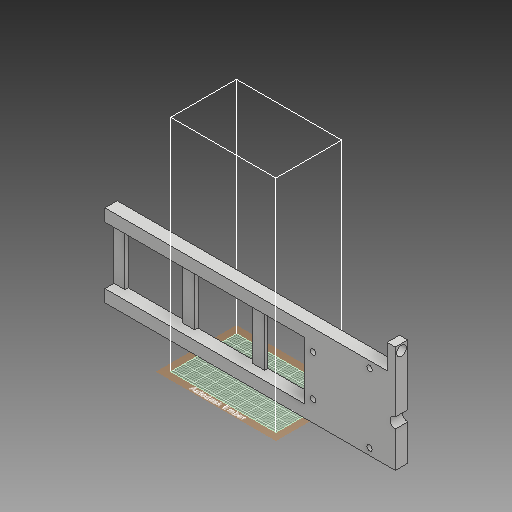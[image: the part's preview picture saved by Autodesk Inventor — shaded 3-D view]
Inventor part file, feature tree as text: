
AUTODESK INVENTOR PART (.ipt)
format: ipt  version: 2018 (Build 220112000, 112)  size: 895,488 bytes
history: native  units: mm
features: sketch x56, extrude x42, fillet x12, hole x8
ambient origin geometry x8: Origin, YZ Plane, XZ Plane, XY Plane, X Axis, Y Axis, Z Axis, Center Point
bodies: Solid1 (feature_tree)
feature tree (118):
  extrude  "Extrusion1"  Depth=50.0mm
  hole  "Hole1"  [1 undecoded]
  hole  "Hole2"  [1 undecoded]
  extrude  "Extrusion2"  Depth=2.0mm
  extrude  "Extrusion3"  Depth=2.0mm
  extrude  "Extrusion4"  Depth=5.0mm
  sketch  "Sketch7"  dims[d25=10.0mm d26=5.0mm]
  extrude  "Extrusion5"  Depth=5.0mm
  extrude  "Extrusion6"  Depth=35.0mm
  extrude  "Extrusion7"  Depth=35.0mm
  extrude  "Extrusion8"  Depth=35.0mm
  extrude  "Extrusion9"  Depth=2.0mm TaperAngle=0.0deg
  extrude  "Extrusion10"  Depth=7.5mm TaperAngle=0.0deg
  extrude  "Extrusion11"  Depth=10.0mm
  extrude  "Extrusion12"  Depth=7.5mm
  fillet  "Fillet1"  Radius=7.5mm
  fillet  "Fillet2"  Radius=25.0mm
  fillet  "Fillet3"  Radius=3.0mm
  fillet  "Fillet4"  Radius=3.2mm
  fillet  "Fillet5"  Radius=2.1mm
  fillet  "Fillet6"  Radius=5.5mm
  extrude  "Extrusion13"  Depth=92.5mm TaperAngle=0.0deg
  sketch  "Sketch17"  dims[d58=4.25mm d59=241.0mm d60=0.0mm]
  hole  "Hole3"  [1 undecoded]
  hole  "Hole4"  [1 undecoded]
  extrude  "Extrusion14"  Depth=5.0mm
  extrude  "Extrusion15"  Depth=2.5mm TaperAngle=0.0deg
  extrude  "Extrusion16"  Depth=6.35mm
  extrude  "Extrusion17"  Depth=2.5mm
  extrude  "Extrusion18"  Depth=14.55mm TaperAngle=0.0deg
  extrude  "Extrusion19"  Depth=0.1mm
  extrude  "Extrusion20"  Depth=3.25mm
  extrude  "Extrusion21"  Depth=3.25mm
  hole  "Hole5"  [1 undecoded]
  extrude  "Extrusion22"  Depth=2.0mm
  extrude  "Extrusion23"  Depth=15.0mm
  extrude  "Extrusion24"  Depth=10.0mm TaperAngle=0.0deg
  hole  "Hole6"  [1 undecoded]
  extrude  "Extrusion25"  Depth=100.0mm TaperAngle=0.0deg
  extrude  "Extrusion26"  Depth=2.0mm TaperAngle=0.0deg
  extrude  "Extrusion27"  Depth=3.3mm
  extrude  "Extrusion28"  Depth=3.3mm
  hole  "Hole7"  [1 undecoded]
  extrude  "Extrusion29"  Depth=2.0mm
  extrude  "Extrusion30"  Depth=17.0mm
  hole  "Hole8"  [1 undecoded]
  extrude  "Extrusion31"  Depth=21.0mm
  extrude  "Extrusion32"  Depth=10.0mm
  fillet  "Fillet7"  Radius=3.3mm
  fillet  "Fillet8"  Radius=10.0mm
  extrude  "Extrusion33"  Depth=5.0mm
  extrude  "Extrusion34"  Depth=5.0mm
  sketch  "Sketch45"  dims[d149=10.0mm d150=17.5mm d151=0.0mm]
  sketch  "Sketch46"  dims[d152=5.0mm]
  extrude  "Extrusion35"  Depth=10.0mm TaperAngle=0.0deg
  extrude  "Extrusion36"  Depth=2.0mm TaperAngle=0.0deg
  extrude  "Extrusion37"  Depth=3.75mm
  extrude  "Extrusion38"  Depth=3.75mm
  fillet  "Fillet9"  Radius=3.75mm
  extrude  "Extrusion39"  Depth=10.0mm TaperAngle=0.0deg
  fillet  "Fillet10"  Radius=2.0mm
  sketch  "Sketch52"  dims[d181=5.0mm d182=15.0mm d183=0.0mm]
  extrude  "Extrusion40"  Depth=15.0mm TaperAngle=0.0deg
  sketch  "Sketch54"  dims[d185=6.0mm d186=6.0mm d187=4.0mm d188=2.0mm d189=90.0deg d190=15.0mm d191=0.0mm d192=17.5mm d193=0.0mm]
  extrude  "Extrusion41"  Depth=15.0mm TaperAngle=0.0deg
  extrude  "Extrusion42"  Depth=47.5mm
  fillet  "Fillet11"  Radius=20.0mm
  fillet  "Fillet12"  Radius=5.0mm
  sketch  "Sketch1"  dims[d0=50.0mm d1=50.0mm]
  sketch  "Sketch2"  dims[d2=240.0mm d3=7.5mm]
  sketch  "Sketch3"  dims[d4=7.5mm d5=7.5mm d6=0.0mm]
  sketch  "Sketch4"  dims[d7=6.35mm d8=6.0mm d9=4.0mm d10=2.0mm d11=90.0deg d12=8.0mm d13=20.594885mm d14=25.0mm]
  sketch  "Sketch5"  dims[d15=3.3mm d16=6.0mm d17=4.0mm d18=2.0mm d19=90.0deg d20=8.0mm d21=20.594885mm d22=25.0mm]
  sketch  "Sketch6"  dims[d23=180.0deg d24=5.0mm]
  sketch  "Sketch8"  dims[d27=17.5mm d28=0.0mm d30=35.0mm]
  sketch  "Sketch9"  dims[d31=35.0mm d32=35.0mm]
  sketch  "Sketch10"  dims[d33=35.0mm d34=35.0mm]
  sketch  "Sketch11"  dims[d35=35.0mm d36=2.0mm d37=0.0mm]
  sketch  "Sketch12"  dims[d38=10.0mm d39=7.5mm d40=0.0mm]
  sketch  "Sketch13"  dims[d41=100.0mm d42=10.0mm]
  sketch  "Sketch14"  dims[d43=7.5mm d44=0.0mm d45=7.5mm d46=7.5mm d47=25.0mm d48=0.0mm d49=3.0mm d50=3.2mm d51=2.1mm d52=5.5mm]
  sketch  "Sketch15"  dims[d53=3.3mm d54=92.5mm d55=0.0mm]
  sketch  "Sketch16"  dims[d56=5.5mm d57=3.3mm]
  sketch  "Sketch18"  dims[d61=4.44mm d62=5.0mm]
  sketch  "Sketch19"  dims[d63=2.5mm d64=91.25mm d65=0.0mm]
  sketch  "Sketch20"  dims[d66=30.0mm d67=6.35mm]
  sketch  "Sketch21"  dims[d68=3.8mm d69=0.0mm d70=2.5mm]
  sketch  "Sketch22"  dims[d71=14.55mm d72=0.0mm d73=14.55mm d74=0.0mm]
  sketch  "Sketch23"  dims[d75=0.1mm d76=0.1mm]
  sketch  "Sketch24"  dims[d77=3.25mm d78=3.25mm]
  sketch  "Sketch25"  dims[d79=3.25mm d80=3.25mm]
  sketch  "Sketch26"  dims[d81=35.0mm d82=10.0mm]
  sketch  "Sketch27"  dims[d83=2.0mm d84=0.0mm d85=3.6mm]
  sketch  "Sketch28"  dims[d86=3.6mm]
  sketch  "Sketch29"  dims[d87=3.3mm d88=6.0mm d89=4.0mm d90=2.0mm d91=90.0deg d92=15.0mm d93=20.594885mm]
  sketch  "Sketch30"  dims[d94=3.3mm d95=6.0mm d96=4.0mm d97=2.0mm d98=90.0deg d99=15.0mm d100=20.594885mm d101=6.0mm]
  sketch  "Sketch31"  dims[d102=20.0mm d103=0.0mm d104=10.0mm d105=0.0mm]
  sketch  "Sketch32"  dims[d106=2.0mm d107=0.0mm d108=4.0mm]
  sketch  "Sketch33"  dims[d109=100.0mm d110=0.0mm d111=100.0mm d112=0.0mm]
  sketch  "Sketch34"  dims[d113=5.0mm d114=2.0mm d115=0.0mm]
  sketch  "Sketch35"  dims[d116=3.3mm d117=3.3mm]
  sketch  "Sketch36"  dims[d118=3.3mm d119=3.3mm]
  sketch  "Sketch37"  dims[d120=2.0mm d121=0.0mm d122=5.5mm d123=0.0mm]
  sketch  "Sketch38"  dims[d124=3.3mm d125=6.0mm d126=4.0mm d127=2.0mm d128=90.0deg d129=8.0mm d130=20.594885mm d131=42.0mm]
  sketch  "Sketch39"  dims[d132=17.0mm d133=21.0mm]
  sketch  "Sketch40"  dims[d135=8.5mm d136=15.825mm]
  sketch  "Sketch41"  dims[d137=3.5mm d138=21.0mm]
  sketch  "Sketch42"  dims[d139=3.3mm d140=3.3mm d141=3.3mm d142=10.0mm d143=0.0mm]
  sketch  "Sketch43"  dims[d144=7.5mm d145=0.0mm d146=5.0mm]
  sketch  "Sketch44"  dims[d147=10.0mm d148=5.0mm]
  sketch  "Sketch47"  dims[d153=7.0mm d154=6.0mm d155=4.0mm d156=2.0mm d157=90.0deg d158=8.0mm d159=20.594885mm d160=17.5mm d161=0.0mm]
  sketch  "Sketch48"  dims[d162=170.5mm d163=0.0mm d164=3.75mm]
  sketch  "Sketch49"  dims[d165=3.75mm d166=3.75mm d167=3.75mm]
  sketch  "Sketch50"  dims[d168=10.0mm d169=0.0mm d170=100.0mm d171=0.0mm]
  sketch  "Sketch51"  dims[d172=5.0mm d173=6.0mm d174=4.0mm d175=2.0mm d176=90.0deg d177=15.0mm d178=0.0mm d179=2.0mm d180=0.0mm]
  sketch  "Sketch53"  dims[d184=7.5mm]
  sketch  "Sketch55"  dims[d194=23.75mm d195=47.5mm d200=20.0mm d203=5.0mm]
  sketch  "Sketch56"  dims[d204=5.0mm d205=29.0mm d206=29.0mm d207=7.5mm d208=0.0mm d209=4.0mm d210=4.0mm d211=2.0mm d212=0.0mm d213=12.0mm d214=2.0mm d215=0.0mm d216=7.5mm d217=7.5mm d218=20.0mm d219=0.0mm d220=20.0mm d221=3.3mm d222=20.0mm d223=0.0mm d224=100.0mm d225=0.0mm d226=56.043mm d227=56.043mm d228=3.0mm d229=74.0mm d230=3.0mm d231=77.0mm d232=3.0mm d233=74.0mm d234=3.0mm d235=1.0mm d236=0.0mm d237=2.0mm d238=56.043mm d239=56.043mm d240=56.043mm d241=3.0mm d242=3.0mm d243=1.0mm d244=0.0mm d245=2.0mm d246=1.0mm d247=0.0mm d248=7.5mm d249=0.0mm d250=6.35mm d251=7.5mm d252=0.0mm d253=2.0mm d254=2.0mm]
note: 8 required parameter values undecoded (feature->parameter linkage not recoverable at this tier; creation-order binding heuristic only, values carry confidence <= 0.55)
